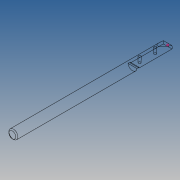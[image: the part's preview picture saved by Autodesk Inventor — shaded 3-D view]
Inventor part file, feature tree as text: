
AUTODESK INVENTOR PART (.ipt)
format: ipt  version: 2018.3 (Build 223284000, 284)  size: 128,000 bytes
history: native  units: in
note: dims shown in document units (in); Inventor stores cm internally (conversion verified against a paired STEP export)
features: sketch x5, extrude x3, hole x1, chamfer x1
ambient origin geometry x8: Origin, YZ Plane, XZ Plane, XY Plane, X Axis, Y Axis, Z Axis, Center Point
bodies: Solid1 (feature_tree)
feature tree (10):
  sketch  "Sketch1"  dims[d0=0.25in d1=4.3in d2=0.0in]
  extrude  "Extrusion1"  Depth=4.3in TaperAngle=0.0deg
  extrude  "Extrusion2"  Depth=0.02in
  hole  "Hole1"  [1 undecoded]
  chamfer  "Chamfer1"  Distance=1.0in
  extrude  "Extrusion3"  Depth=0.125in
  sketch  "Sketch2"  dims[d3=0.975in d4=0.02in]
  sketch  "Sketch3"  dims[d5=0.06in d6=0.156in d7=1.0in d8=0.0in]
  sketch  "Sketch4"  dims[d9=0.03in d10=0.125in d11=45.0deg d13=0.63in]
  sketch  "Sketch5"  dims[d14=0.4331in d15=0.062in d16=0.157in d17=0.375in d18=0.25in d19=0.5635in d20=0.248in d21=0.8108in d22=0.076in d24=1.0in d25=0.0in d26=0.08in d27=15.0deg]
note: 1 required parameter value undecoded (feature->parameter linkage not recoverable at this tier; creation-order binding heuristic only, values carry confidence <= 0.55)
